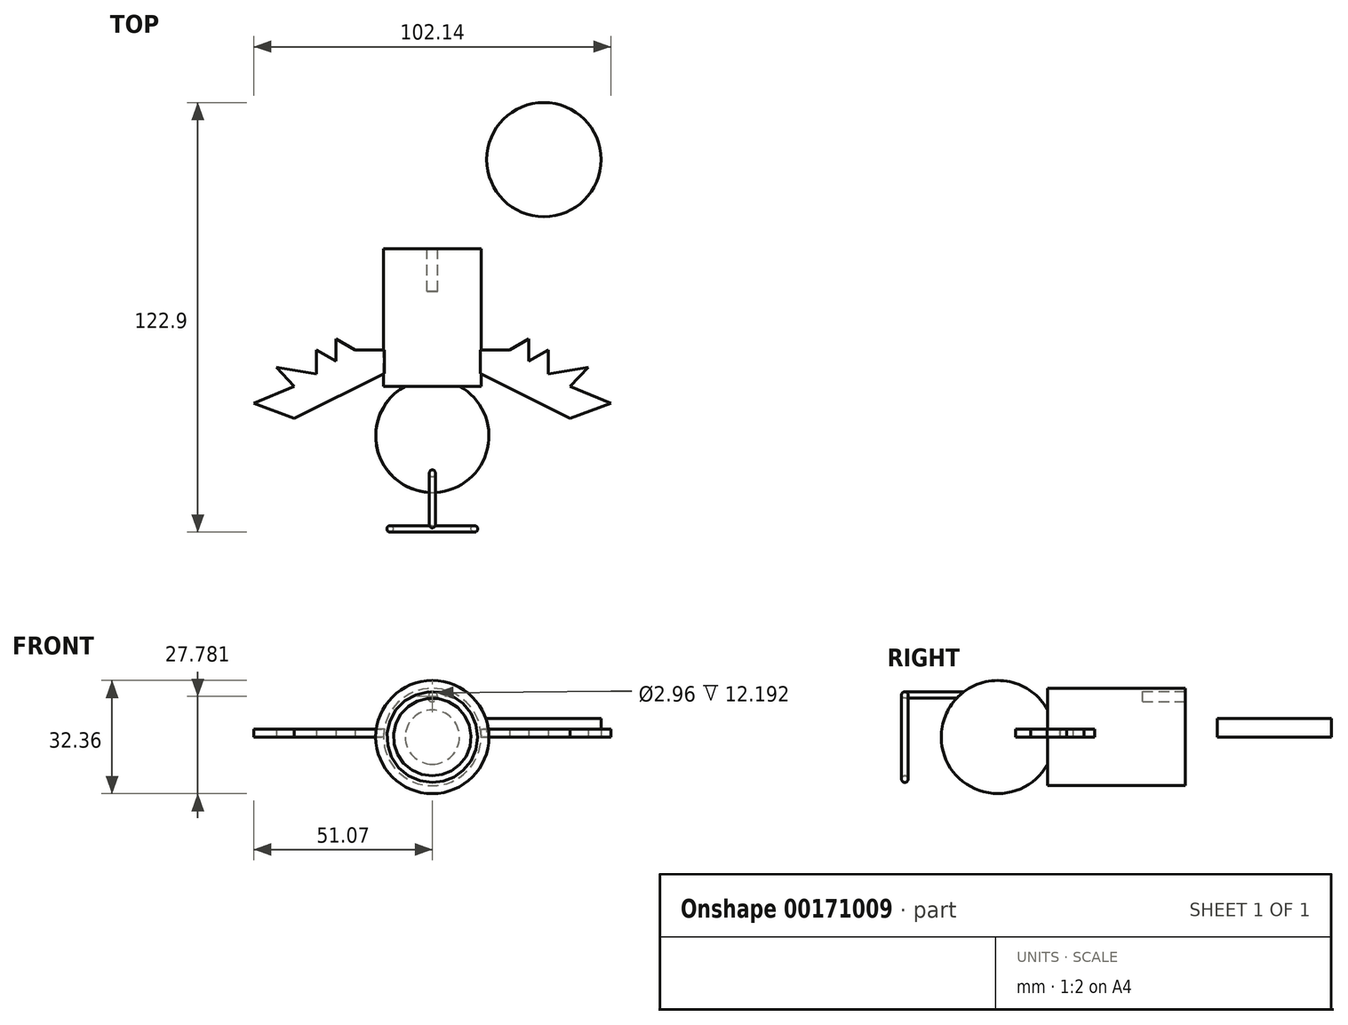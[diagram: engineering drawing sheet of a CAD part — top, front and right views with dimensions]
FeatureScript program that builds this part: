
annotation { "Feature Type Name" : "Feature", "Feature Type Description" : "" }
export const myFeature = defineFeature(function(context is Context, id is Id, definition is map)
    precondition{}
    {
        {
            var Q0;
            Q0=qCreatedBy(makeId("Front.planeOp"),FACE);
            var sketch = newSketch(context, id + "F0", { "sketchPlane" : qUnion([Q0])});
            skCircle(sketch, "E0", {"center": v(0, 0) * mm, "radius": 13.93 * mm});
            skSolve(sketch);
        }
        {
            var Q0;
            Q0=makeQuery(id+"F0.imprint","IMPRINT",FACE,{"disambiguationData":[TD([[makeQuery(id+"F0.imprint","IMPRINT",EDGE,{"derivedFrom":sQuery(id+"F0.wireOp",EDGE,"E0")}),1.0]])]});
            extrude(context, id + "F1", {"entities" : qUnion([Q0]), "depth" : 39.37 * mm});
        }
        {
            var Q0;
            Q0=qCreatedBy(makeId("Top.planeOp"),FACE);
            var sketch = newSketch(context, id + "F2", { "sketchPlane" : qUnion([Q0])});
            skArc(sketch, "E1", {"start": v(0, -69.75) * mm, "mid": v(16.18, -53.57) * mm, "end": v(0, -37.4) * mm});
            skLineSegment(sketch, "E2", {"start": v(0, -69.75) * mm, "end": v(0, -37.4) * mm});
            skSolve(sketch);
        }
        {
            var Q0;
            Q0=makeQuery(id+"F2.imprint","IMPRINT",FACE,{"disambiguationData":[TD([[makeQuery(id+"F2.imprint","IMPRINT",EDGE,{"derivedFrom":sQuery(id+"F2.wireOp",EDGE,"E1")}),1.0]])]});
            var Q1;
            Q1=sQuery(id+"F2.wireOp",EDGE,"E2");
            revolve(context, id + "F3", {"operationType" : NewBodyOperationType.ADD, "entities" : qUnion([Q0]), "axis" : qUnion([Q1]), "revolveType" : RevolveType.FULL});
        }
        {
            var Q0;
            Q0=qCreatedBy(makeId("Top.planeOp"),FACE);
            var sketch = newSketch(context, id + "F4", { "sketchPlane" : qUnion([Q0])});
            skLineSegment(sketch, "E3", {"start": v(11.02, -34.32) * mm, "end": v(39.43, -48.53) * mm});
            skLineSegment(sketch, "E4", {"start": v(39.43, -48.53) * mm, "end": v(51.07, -44.19) * mm});
            skLineSegment(sketch, "E5", {"start": v(51.07, -44.19) * mm, "end": v(39.43, -39.45) * mm});
            skLineSegment(sketch, "E6", {"start": v(39.43, -39.45) * mm, "end": v(44.56, -33.92) * mm});
            skLineSegment(sketch, "E7", {"start": v(44.56, -33.92) * mm, "end": v(33.12, -35.9) * mm});
            skLineSegment(sketch, "E8", {"start": v(33.12, -35.9) * mm, "end": v(33.12, -29) * mm});
            skLineSegment(sketch, "E9", {"start": v(33.12, -29) * mm, "end": v(27.6, -32.15) * mm});
            skLineSegment(sketch, "E10", {"start": v(27.6, -32.15) * mm, "end": v(27.6, -25.84) * mm});
            skLineSegment(sketch, "E11", {"start": v(27.6, -25.84) * mm, "end": v(22.07, -29) * mm});
            skLineSegment(sketch, "E12", {"start": v(22.07, -29) * mm, "end": v(10.03, -29) * mm});
            skLineSegment(sketch, "E13", {"start": v(10.03, -29) * mm, "end": v(11.02, -34.32) * mm});
            skSolve(sketch);
        }
        {
            var Q0;
            Q0 = qSketchRegion(id + "F4", true);
            var Q1;
            Q1=makeQuery(id+"F4.imprint","IMPRINT",FACE,{"disambiguationData":[TD([[makeQuery(id+"F4.imprint","IMPRINT",EDGE,{"derivedFrom":sQuery(id+"F4.wireOp",EDGE,"E3")}),1.0]])]});
            extrude(context, id + "F5", {"entities" : qUnion([Q0, Q1]), "operationType" : NewBodyOperationType.ADD, "depth" : 2.3 * mm});
        }
        {
            var Q0;
            Q0=qCreatedBy(makeId("Front.planeOp"),FACE);
            var sketch = newSketch(context, id + "F6", { "sketchPlane" : qUnion([Q0])});
            skCircle(sketch, "E14", {"center": v(0, 11.6) * mm, "radius": 1.48 * mm});
            skSolve(sketch);
        }
        {
            var Q0;
            Q0 = qSketchRegion(id + "F6", true);
            extrude(context, id + "F7", {"entities" : qUnion([Q0]), "operationType" : NewBodyOperationType.REMOVE, "depth" : 12.2 * mm});
        }
        {
            var Q0;
            Q0=qCreatedBy(makeId("Front.planeOp"),FACE);
            cPlane(context, id + "F8", {"entities" : qUnion([Q0]), "cplaneType" : CPlaneType.OFFSET, "offset" : 50.8 * mm, "width" : 152.4 * mm, "height" : 152.4 * mm});
        }
        {
            var Q0;
            Q0=qCreatedBy(id+"F8.planeOp",FACE);
            var sketch = newSketch(context, id + "F9", { "sketchPlane" : qUnion([Q0])});
            skCircle(sketch, "E15", {"center": v(0, 12.04) * mm, "radius": 0.9 * mm});
            skSolve(sketch);
        }
        {
            var Q0;
            Q0=makeQuery(id+"F1.opExtrude","SWEPT_BODY",BODY,{"disambiguationData":[OSD([sQuery(id+"F0.wireOp",EDGE,"E0")])]});
            var Q1;
            Q1=qCreatedBy(makeId("Right.planeOp"),FACE);
            mirror(context, id + "F10", {"operationType" : NewBodyOperationType.ADD, "entities" : qUnion([Q0]), "mirrorPlane" : qUnion([Q1])});
        }
        {
            var Q0;
            Q0=qCreatedBy(id+"F8.planeOp",FACE);
            cPlane(context, id + "F11", {"entities" : qUnion([Q0]), "cplaneType" : CPlaneType.OFFSET, "offset" : 28.45 * mm, "width" : 152.4 * mm, "height" : 152.4 * mm});
        }
        {
            var Q0;
            Q0 = qSketchRegion(id + "F9", true);
            extrude(context, id + "F12", {"entities" : qUnion([Q0]), "operationType" : NewBodyOperationType.ADD, "depth" : 29.36 * mm});
        }
        {
            var Q0;
            Q0=qCreatedBy(makeId("Right.planeOp"),FACE);
            var sketch = newSketch(context, id + "F13", { "sketchPlane" : qUnion([Q0])});
            skCircle(sketch, "E16", {"center": v(-80.16, 12.03) * mm, "radius": 0.94 * mm});
            skSolve(sketch);
        }
        {
            var Q0;
            Q0=qCreatedBy(makeId("Top.planeOp"),FACE);
            var sketch = newSketch(context, id + "F14", { "sketchPlane" : qUnion([Q0])});
            skLineSegment(sketch, "E17", {"start": v(0, -67.08) * mm, "end": v(0, -86.09) * mm});
            skSolve(sketch);
        }
        {
            var Q0;
            Q0=makeQuery(id+"F13.imprint","IMPRINT",FACE,{"disambiguationData":[TD([[makeQuery(id+"F13.imprint","IMPRINT",EDGE,{"derivedFrom":sQuery(id+"F13.wireOp",EDGE,"E16")}),1.0]])]});
            var Q1;
            Q1=sQuery(id+"F14.wireOp",EDGE,"E17");
            revolve(context, id + "F15", {"operationType" : NewBodyOperationType.ADD, "entities" : qUnion([Q0]), "axis" : qUnion([Q1]), "revolveType" : RevolveType.FULL});
        }
        {
            var Q0;
            Q0=qCreatedBy(makeId("Top.planeOp"),FACE);
            var sketch = newSketch(context, id + "F16", { "sketchPlane" : qUnion([Q0])});
            skCircle(sketch, "E18", {"center": v(31.9, 25.46) * mm, "radius": 16.34 * mm});
            skSolve(sketch);
        }
        {
            var Q0;
            Q0=makeQuery(id+"F16.imprint","IMPRINT",FACE,{"disambiguationData":[TD([[makeQuery(id+"F16.imprint","IMPRINT",EDGE,{"derivedFrom":sQuery(id+"F16.wireOp",EDGE,"E18")}),1.0]])]});
            extrude(context, id + "F17", {"entities" : qUnion([Q0]), "depth" : 5.33 * mm});
        }
    });
